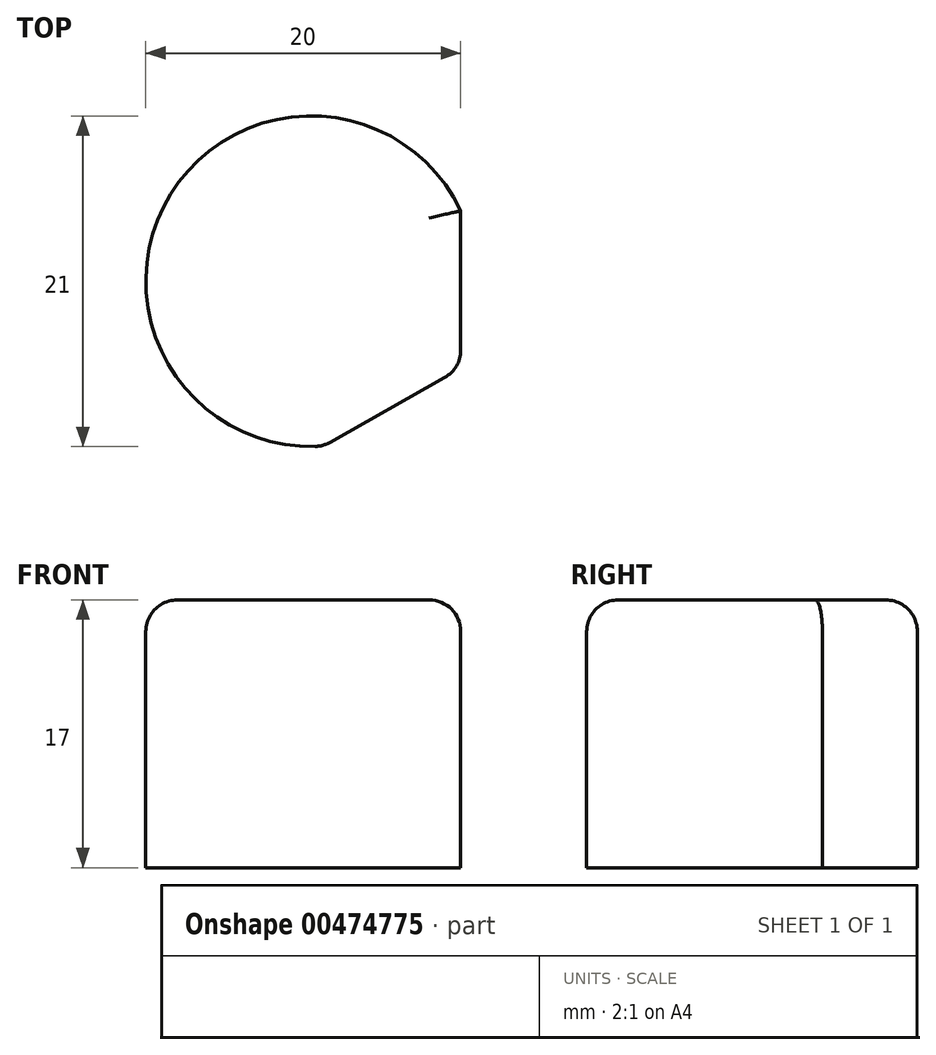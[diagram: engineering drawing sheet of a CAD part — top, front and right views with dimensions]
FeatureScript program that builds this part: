
annotation { "Feature Type Name" : "Feature", "Feature Type Description" : "" }
export const myFeature = defineFeature(function(context is Context, id is Id, definition is map)
    precondition{}
    {
        {
            var Q0;
            Q0=qCreatedBy(makeId("Top.planeOp"),FACE);
            var sketch = newSketch(context, id + "F0", { "sketchPlane" : qUnion([Q0])});
            skArc(sketch, "E0", {"start": v(9.5, 4.47) * mm, "mid": v(-9.07, 5.3) * mm, "end": v(0.78, -10.47) * mm});
            skLineSegment(sketch, "E1", {"start": v(9.5, 4.47) * mm, "end": v(9.5, -5.55) * mm});
            skLineSegment(sketch, "E2", {"start": v(0.78, -10.47) * mm, "end": v(9.5, -5.55) * mm});
            skLineSegment(sketch, "E3", {"start": v(9.5, -5.55) * mm, "end": v(-9.07, 5.3) * mm, "construction": true});
            skSolve(sketch);
        }
        {
            var Q0;
            Q0 = qSketchRegion(id + "F0", true);
            extrude(context, id + "F1", {"entities" : qUnion([Q0]), "depth" : 17 * mm});
        }
        {
            var Q0;
            Q0=makeQuery(id+"F1.opExtrude","CAP_EDGE",EDGE,{"disambiguationData":[OSD([sQuery(id+"F0.wireOp",EDGE,"E0")])],"isStart":false});
            var Q1;
            Q1=makeQuery(id+"F1.opExtrude","CAP_EDGE",EDGE,{"disambiguationData":[OSD([sQuery(id+"F0.wireOp",EDGE,"E2")])],"isStart":false});
            var Q2;
            Q2=makeQuery(id+"F1.opExtrude","CAP_FACE",FACE,{"disambiguationData":[OSD([sQuery(id+"F0.wireOp",EDGE,"E0"),sQuery(id+"F0.wireOp",EDGE,"E1"),sQuery(id+"F0.wireOp",EDGE,"E2")])],"isStart":false});
            var Q3;
            Q3=makeQuery(id+"F1.opExtrude","SWEPT_EDGE",EDGE,{"disambiguationData":[OSD([sQuery(id+"F0.wireOp",EDGE,"E0"),sQuery(id+"F0.wireOp",EDGE,"E2")])]});
            var Q4;
            Q4=makeQuery(id+"F1.opExtrude","SWEPT_EDGE",EDGE,{"disambiguationData":[OSD([sQuery(id+"F0.wireOp",EDGE,"E1"),sQuery(id+"F0.wireOp",EDGE,"E2")])]});
            fillet(context, id + "F2", {"entities" : qUnion([Q0, Q1, Q2, Q3, Q4]), "radius" : 2 * mm, "tangentPropagation" : true, "allowEdgeOverflow" : false});
        }
    });
